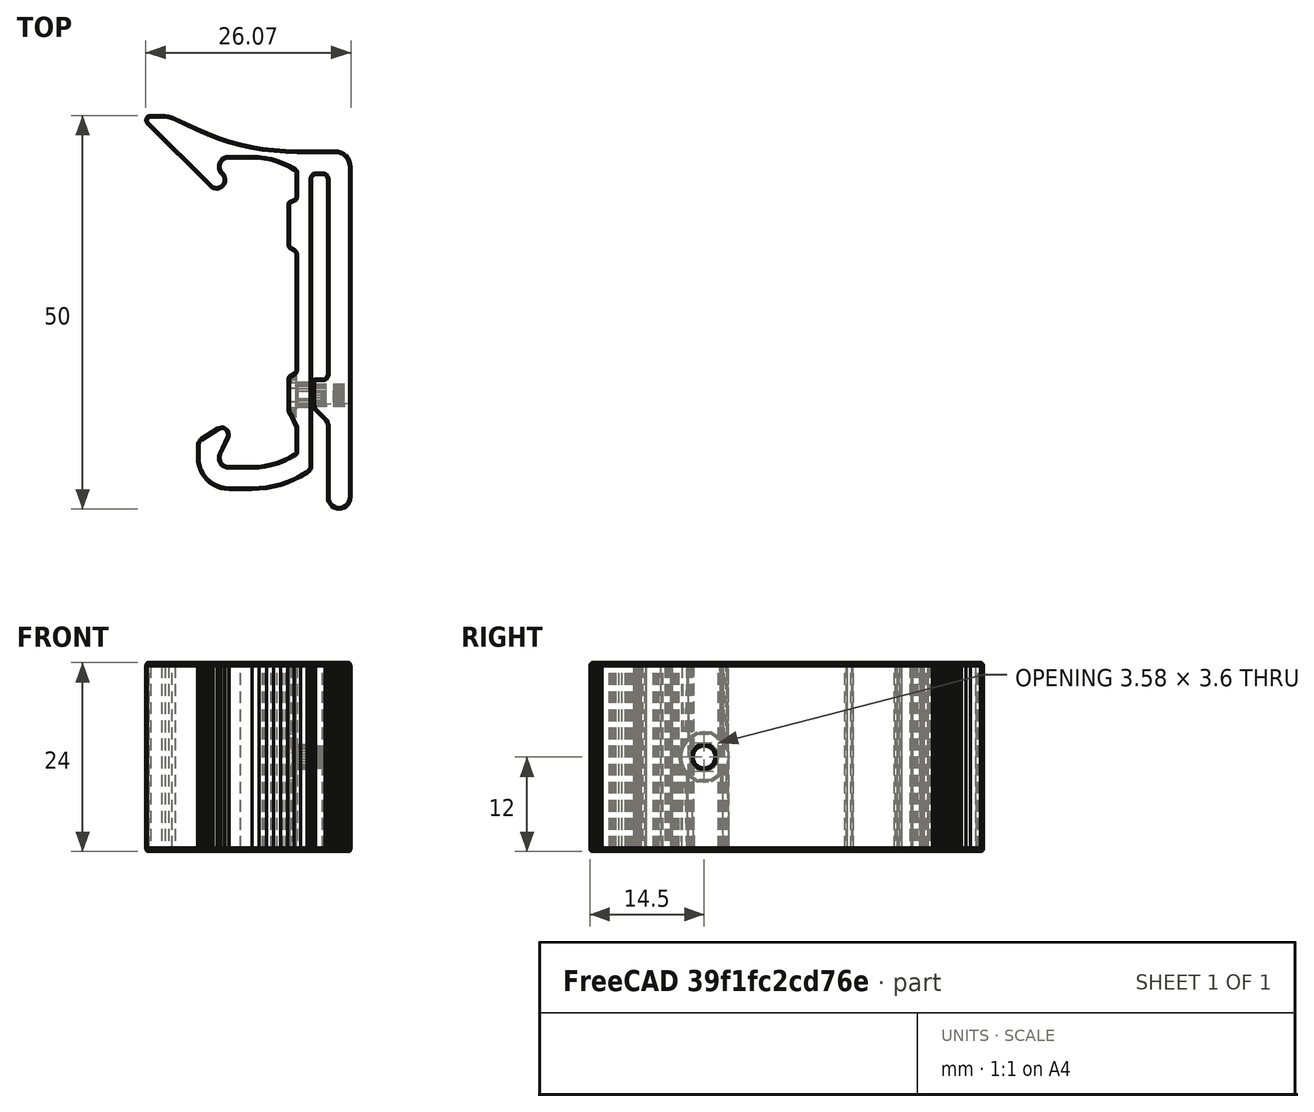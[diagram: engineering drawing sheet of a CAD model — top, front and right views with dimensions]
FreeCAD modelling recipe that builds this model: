
FCSTD DOCUMENT  (FreeCAD 0.21R33771 (Git))
Label: PenelopeClip
License: All rights reserved
LicenseURL: http://en.wikipedia.org/wiki/All_rights_reserved
objects: Part::Refine×1, PartDesign::FeatureBase×1, Sketcher::SketchObject×1, PartDesign::Body×1
note: 4 computed .brp shape members not serialized (recipe doc carries the construction recipe); baked Part::Feature solids carry a one-line shape summary decoded from their .brp

FEATURE [Part::Refine] Alley_Cat_TBeam_Molle_Clip001_solid001  label="Alley_Cat_TBeam_Molle_Clip001 (Solid)001"
FEATURE [PartDesign::FeatureBase] BaseFeature
  BaseFeature = -> Alley_Cat_TBeam_Molle_Clip001_solid001
FEATURE [Sketcher::SketchObject] Sketch
  FullyConstrained = true
  MapMode = 5
  Support = -> [XY_Plane]
  sketch-geometry (67):
    g0: LineSegment StartX=0 StartY=0 StartZ=0 EndX=0 EndY=42.04 EndZ=0
    g1: ArcOfCircle CenterX=-2 CenterY=42.04 CenterZ=0 NormalX=0 NormalY=0 NormalZ=1 AngleXU=0 Radius=2 StartAngle=1e-15 EndAngle=1.57049
    g2: LineSegment StartX=-1.99938 StartY=44.04 StartZ=0 EndX=-6.83938 EndY=44.0415 EndZ=0
    g3: LineSegment StartX=-6.83938 StartY=44.0415 StartZ=0 EndX=-8.29938 EndY=44.0804 EndZ=0
    g4: LineSegment StartX=-8.29938 StartY=44.0804 StartZ=0 EndX=-9.74938 EndY=44.1804 EndZ=0
    g5: LineSegment StartX=-9.74938 StartY=44.1804 StartZ=0 EndX=-11.1894 EndY=44.3604 EndZ=0
    g6: LineSegment StartX=-11.1894 StartY=44.3604 StartZ=0 EndX=-12.6294 EndY=44.6004 EndZ=0
    g7: LineSegment StartX=-12.6294 StartY=44.6004 StartZ=0 EndX=-14.0394 EndY=44.9204 EndZ=0
    g8: LineSegment StartX=-14.0394 StartY=44.9204 StartZ=0 EndX=-15.4494 EndY=45.3004 EndZ=0
    g9: LineSegment StartX=-15.4494 StartY=45.3004 StartZ=0 EndX=-16.8394 EndY=45.7504 EndZ=0
    g10: LineSegment StartX=-16.8394 StartY=45.7504 StartZ=0 EndX=-18.1994 EndY=46.2704 EndZ=0
    g11: LineSegment StartX=-18.1994 StartY=46.2704 StartZ=0 EndX=-19.5294 EndY=46.8504 EndZ=0
    g12: LineSegment StartX=-19.5294 StartY=46.8504 StartZ=0 EndX=-22.3294 EndY=48.1604 EndZ=0
    g13: ArcOfCircle CenterX=-24.0626 CenterY=44.4558 CenterZ=0 NormalX=0 NormalY=0 NormalZ=1 AngleXU=0 Radius=4.09 StartAngle=1.13319 EndAngle=1.51939
    g14: LineSegment StartX=-23.8525 StartY=48.5404 StartZ=0 EndX=-25.2925 EndY=48.5404 EndZ=0
    g15: ArcOfCircle CenterX=-25.2925 CenterY=47.9404 CenterZ=0 NormalX=0 NormalY=0 NormalZ=1 AngleXU=0 Radius=0.6 StartAngle=1.5708 EndAngle=3.9406
    g16: LineSegment StartX=-25.7109 StartY=47.5104 StartZ=0 EndX=-17.7309 EndY=39.5304 EndZ=0
    g17: ArcOfCircle CenterX=-16.8965 CenterY=40.3647 CenterZ=0 NormalX=0 NormalY=0 NormalZ=1 AngleXU=0 Radius=1.18 StartAngle=3.92699 EndAngle=6.83204
    g18: LineSegment StartX=-15.8898 StartY=40.9804 StartZ=0 EndX=-16.0498 EndY=41.2104 EndZ=0
    g19: LineSegment StartX=-16.0498 StartY=41.2104 StartZ=0 EndX=-16.1898 EndY=41.3504 EndZ=0
    g20: ArcOfCircle CenterX=-15.5181 CenterY=42.0221 CenterZ=0 NormalX=0 NormalY=0 NormalZ=1 AngleXU=0 Radius=0.95 StartAngle=2.92059 EndAngle=3.92699
    g21: ArcOfCircle CenterX=-15.3132 CenterY=41.9761 CenterZ=0 NormalX=0 NormalY=0 NormalZ=1 AngleXU=0 Radius=1.16 StartAngle=1.67012 EndAngle=2.92059
    g22: LineSegment StartX=-15.4282 StartY=43.1304 StartZ=0 EndX=-12.4682 EndY=43.1304 EndZ=0
    g23: ArcOfCircle CenterX=-12.4682 CenterY=33.0904 CenterZ=0 NormalX=0 NormalY=0 NormalZ=1 AngleXU=0 Radius=10.04 StartAngle=1.0134 EndAngle=1.5708
    g24: LineSegment StartX=-7.1573 StartY=41.6107 StartZ=0 EndX=-7.10385 EndY=41.5774 EndZ=0
    g25: ArcOfCircle CenterX=-7.20965 CenterY=41.4076 CenterZ=0 NormalX=0 NormalY=0 NormalZ=1 AngleXU=0 Radius=0.2 StartAngle=0.0595829 EndAngle=1.0134
    g26: LineSegment StartX=-7.01 StartY=41.4195 StartZ=0 EndX=-7.01 EndY=38.2495 EndZ=0
    g27: ArcOfCircle CenterX=-7.4 CenterY=38.2495 CenterZ=0 NormalX=0 NormalY=0 NormalZ=1 AngleXU=0 Radius=0.39 StartAngle=5.10718 EndAngle=6.28319
    g28: LineSegment StartX=-7.25 StartY=37.8895 StartZ=0 EndX=-7.78 EndY=37.6395 EndZ=0
    g29: ArcOfCircle CenterX=-7.60935 CenterY=37.2778 CenterZ=0 NormalX=0 NormalY=0 NormalZ=1 AngleXU=0 Radius=0.4 StartAngle=2.01155 EndAngle=3.35826
    g30: LineSegment StartX=-8 StartY=37.1918 StartZ=0 EndX=-8 EndY=31.9818 EndZ=0
    g31: ArcOfCircle CenterX=-7.6 CenterY=31.9818 CenterZ=0 NormalX=0 NormalY=0 NormalZ=1 AngleXU=0 Radius=0.4 StartAngle=3.14159 EndAngle=4.1509
    g32: LineSegment StartX=-7.81298 StartY=31.6432 StartZ=0 EndX=-7.19298 EndY=31.2532 EndZ=0
    g33: ArcOfCircle CenterX=-7.39531 CenterY=30.9315 CenterZ=0 NormalX=0 NormalY=0 NormalZ=1 AngleXU=0 Radius=0.38 StartAngle=6.23489 EndAngle=7.29249
    g34: LineSegment StartX=-7.01575 StartY=30.9132 StartZ=0 EndX=-7.01575 EndY=16.1232 EndZ=0
    g35: ArcOfCircle CenterX=-7.38575 CenterY=16.1232 CenterZ=0 NormalX=0 NormalY=0 NormalZ=1 AngleXU=0 Radius=0.37 StartAngle=5.24441 EndAngle=6.28319
    g36: LineSegment StartX=-7.19806 StartY=15.8043 StartZ=0 EndX=-7.81806 EndY=15.4043 EndZ=0
    g37: ArcOfCircle CenterX=-7.59579 CenterY=15.0598 CenterZ=0 NormalX=0 NormalY=0 NormalZ=1 AngleXU=0 Radius=0.41 StartAngle=2.14376 EndAngle=3.15495
    g38: LineSegment StartX=-8.00575 StartY=15.0543 StartZ=0 EndX=-8.00575 EndY=11.1143 EndZ=0
    g39: ArcOfCircle CenterX=-7.46575 CenterY=11.1143 CenterZ=0 NormalX=0 NormalY=0 NormalZ=1 AngleXU=0 Radius=0.54 StartAngle=3.14159 EndAngle=3.73722
    g40: LineSegment StartX=-7.91277 StartY=10.8114 StartZ=0 EndX=-7.57277 EndY=10.1814 EndZ=0
    g41: LineSegment StartX=-7.57277 StartY=10.1814 StartZ=0 EndX=-7.26277 EndY=9.53138 EndZ=0
    g42: LineSegment StartX=-7.26277 StartY=9.53138 StartZ=0 EndX=-7.00277 EndY=8.90138 EndZ=0
    g43: LineSegment StartX=-7.00277 StartY=8.90138 StartZ=0 EndX=-7.00277 EndY=5.71138 EndZ=0
    g44: ArcOfCircle CenterX=-7.20277 CenterY=5.71138 CenterZ=0 NormalX=0 NormalY=0 NormalZ=1 AngleXU=0 Radius=0.2 StartAngle=5.28586 EndAngle=6.28319
    g45: LineSegment StartX=-7.09426 StartY=5.54337 StartZ=0 EndX=-7.86426 EndY=5.10337 EndZ=0
    g46: LineSegment StartX=-7.86426 StartY=5.10337 StartZ=0 EndX=-8.59426 EndY=4.74337 EndZ=0
    g47: LineSegment StartX=-8.59426 StartY=4.74337 StartZ=0 EndX=-9.36426 EndY=4.45337 EndZ=0
    g48: LineSegment StartX=-9.36426 StartY=4.45337 StartZ=0 EndX=-10.1543 EndY=4.22337 EndZ=0
    g49: LineSegment StartX=-10.1543 StartY=4.22337 StartZ=0 EndX=-10.9543 EndY=4.05337 EndZ=0
    g50: LineSegment StartX=-10.9543 StartY=4.05337 StartZ=0 EndX=-11.7643 EndY=3.95489 EndZ=0
    g51: LineSegment StartX=-11.7643 StartY=3.95489 StartZ=0 EndX=-12.5743 EndY=3.91785 EndZ=0
    g52: LineSegment StartX=-12.5743 StartY=3.91785 StartZ=0 EndX=-15.5443 EndY=3.91785 EndZ=0
    g53: ArcOfCircle CenterX=-15.5443 CenterY=5.01785 CenterZ=0 NormalX=0 NormalY=0 NormalZ=1 AngleXU=0 Radius=1.1 StartAngle=2.71189 EndAngle=4.71239
    g54: LineSegment StartX=-16.5443 StartY=5.47611 StartZ=0 EndX=-15.5443 EndY=7.58611 EndZ=0
    g55: ArcOfCircle CenterX=-16.4118 CenterY=7.99725 CenterZ=0 NormalX=0 NormalY=0 NormalZ=1 AngleXU=0 Radius=0.96 StartAngle=5.84061 EndAngle=8.42102
    g56: LineSegment StartX=-16.9274 StartY=8.80701 StartZ=0 EndX=-19.0474 EndY=7.45701 EndZ=0
    g57: ArcOfCircle CenterX=-18.5049 CenterY=6.60508 CenterZ=0 NormalX=0 NormalY=0 NormalZ=1 AngleXU=0 Radius=1.01 StartAngle=2.13783 EndAngle=3.1405
    g58: LineSegment StartX=-19.5149 StartY=6.60618 StartZ=0 EndX=-19.5166 EndY=5.02618 EndZ=0
    g59: ArcOfCircle CenterX=-15.5066 CenterY=5.02179 CenterZ=0 NormalX=0 NormalY=0 NormalZ=1 AngleXU=0 Radius=4.01 StartAngle=3.1405 EndAngle=4.7137
    g60: LineSegment StartX=-15.5014 StartY=1.01179 StartZ=0 EndX=-12.5814 EndY=1.01562 EndZ=0
    g61: ArcOfCircle CenterX=-12.5986 CenterY=14.1356 CenterZ=0 NormalX=0 NormalY=0 NormalZ=1 AngleXU=0 Radius=13.12 StartAngle=4.7137 EndAngle=5.27671
    g62: ArcOfCircle CenterX=-6.2768 CenterY=4.14825 CenterZ=0 NormalX=0 NormalY=0 NormalZ=1 AngleXU=0 Radius=1.3 StartAngle=5.27671 EndAngle=6.12215
    g63: LineSegment StartX=-4.99361 StartY=3.93981 StartZ=0 EndX=-4.99361 EndY=14.9198 EndZ=0
    g64: ArcOfCircle CenterX=-4.89575 CenterY=14.9198 CenterZ=0 NormalX=0 NormalY=0 NormalZ=1 AngleXU=0 Radius=0.09786 StartAngle=0.207791 EndAngle=3.14159
    g65: LineSegment StartX=-4.8 StartY=14.94 StartZ=0 EndX=-4.8 EndY=0 EndZ=0
    g66: LineSegment StartX=-4.8 StartY=0 StartZ=0 EndX=0 EndY=0 EndZ=0
  constraints (194):
    c: Vertical(g0)
    c: Tangent(g0,g1) = -1.5708
    c: Tangent(g1,g2) = -1.5708
    c: Coincident(g2,g3)
    c: Coincident(g3,g4)
    c: Coincident(g4,g5)
    c: Coincident(g5,g6)
    c: Coincident(g6,g7)
    c: Coincident(g7,g8)
    c: Coincident(g8,g9)
    c: Coincident(g9,g10)
    c: Coincident(g10,g11)
    c: Coincident(g11,g12)
    c: Tangent(g12,g13) = -1.5708
    c: Coincident(g13,g14)
    c: Horizontal(g14)
    c: Tangent(g14,g15) = -1.5708
    c: Coincident(g15,g16)
    c: Tangent(g16,g17) = -1.5708
    c: Coincident(g17,g18)
    c: Coincident(g18,g19)
    c: Tangent(g19,g20) = 1.5708
    c: Tangent(g20,g21) = -1.5708
    c: Coincident(g21,g22)
    c: Horizontal(g22)
    c: Tangent(g22,g23) = 1.5708
    c: Tangent(g23,g24) = 1.5708
    c: Tangent(g24,g25) = 1.5708
    c: Coincident(g25,g26)
    c: Vertical(g26)
    c: Tangent(g26,g27) = 1.5708
    c: Coincident(g27,g28)
    c: Tangent(g28,g29) = -1.5708
    c: Coincident(g29,g30)
    c: Vertical(g30)
    c: Tangent(g30,g31) = -1.5708
    c: Tangent(g31,g32) = -1.5708
    c: Tangent(g32,g33) = 1.5708
    c: Coincident(g33,g34)
    c: Vertical(g34)
    c: Tangent(g34,g35) = 1.5708
    c: Coincident(g35,g36)
    c: Tangent(g36,g37) = -1.5708
    c: Coincident(g37,g38)
    c: Vertical(g38)
    c: Tangent(g38,g39) = -1.5708
    c: Coincident(g39,g40)
    c: Coincident(g40,g41)
    c: Coincident(g41,g42)
    c: Coincident(g42,g43)
    c: Vertical(g43)
    c: Tangent(g43,g44) = 1.5708
    c: Coincident(g44,g45)
    c: Coincident(g45,g46)
    c: Coincident(g46,g47)
    c: Coincident(g47,g48)
    c: Coincident(g48,g49)
    c: Coincident(g49,g50)
    c: Coincident(g50,g51)
    c: Coincident(g51,g52)
    c: Horizontal(g52)
    c: Tangent(g52,g53) = 1.5708
    c: Coincident(g53,g54)
    c: Tangent(g54,g55) = -1.5708
    c: Tangent(g55,g56) = -1.5708
    c: Tangent(g56,g57) = -1.5708
    c: Tangent(g57,g58) = -1.5708
    c: Tangent(g58,g59) = -1.5708
    c: Tangent(g59,g60) = -1.5708
    c: Tangent(g60,g61) = -1.5708
    c: Tangent(g61,g62) = -1.5708
    c: Coincident(g62,g63)
    c: Vertical(g63)
    c: Tangent(g63,g64) = 1.5708
    c: Coincident(g64,g65)
    c: Vertical(g65)
    c: Coincident(g65,g66)
    c: Coincident(g66,g0)
    c: Horizontal(g66)
    c: Radius(g1) = 2
    c: Radius(g15) = 0.6
    c: Radius(g17) = 1.18
    c: Radius(g20) = 0.95
    c: Radius(g21) = 1.16
    c: Radius(g25) = 0.2
    c: Radius(g27) = 0.39
    c: Radius(g29) = 0.4
    c: Radius(g31) = 0.4
    c: Radius(g33) = 0.38
    c: Radius(g35) = 0.37
    c: Radius(g37) = 0.41
    c: Radius(g39) = 0.54
    c: Radius(g44) = 0.2
    c: Radius(g55) = 0.96
    c: Radius(g57) = 1.01
    c: Radius(g53) = 1.1
    c: Radius(g59) = 4.01
    c: Radius(g61) = 13.12
    c: Radius(g62) = 1.3
    c: Radius(g64) = 0.09786
    c: DistanceY(g0,g0) = 42.04
    c: DistanceY(g65,g65) = 14.94
    c: DistanceY(g63,g63) = 10.98
    c: DistanceY(g45,g45) = 0.44
    c: DistanceY(g46,g46) = 0.36
    c: DistanceY(g47,g47) = 0.29
    c: DistanceY(g48,g48) = 0.23
    c: DistanceY(g49,g49) = 0.17
    c: DistanceY(g50,g50) = 0.09848
    c: DistanceY(g51,g51) = 0.03704
    c: DistanceY(g54,g54) = 2.11
    c: DistanceY(g56,g56) = 1.35
    c: DistanceY(g58,g58) = 1.58
    c: DistanceY(g38,g38) = 3.94
    c: DistanceY(g40,g40) = 0.63
    c: DistanceY(g41,g41) = 0.65
    c: DistanceY(g42,g42) = 0.63
    c: DistanceY(g34,g34) = 14.79
    c: DistanceY(g32,g32) = 0.39
    c: DistanceY(g30,g30) = 5.21
    c: DistanceY(g26,g26) = 3.17
    c: DistanceY(g16,g16) = 7.98
    c: Radius(g13) = 4.09
    c: DistanceY(g12,g12) = 1.31
    c: DistanceY(g11,g11) = 0.58
    c: DistanceY(g10,g10) = 0.52
    c: DistanceY(g9,g9) = 0.45
    c: DistanceY(g8,g8) = 0.38
    c: DistanceY(g7,g7) = 0.32
    c: DistanceY(g6,g6) = 0.24
    c: DistanceY(g5,g5) = 0.18
    c: DistanceY(g4,g4) = 0.1
    c: DistanceY(g3,g3) = 0.03887
    c: DistanceY(g2,g2) = 0.00149
    c: Radius(g23) = 10.04
    c: DistanceX(g66,g66) = 4.8
    c: DistanceX(g60,g60) = 2.92
    c: DistanceY(g60,g60) = 0.00383
    c: DistanceX(g58,g58) = 0.00173
    c: DistanceX(g56,g56) = 2.12
    c: DistanceX(g54,g54) = 1
    c: DistanceX(g52,g52) = 2.97
    c: DistanceX(g51,g51) = 0.81
    c: DistanceX(g50,g50) = 0.81
    c: DistanceX(g49,g49) = 0.8
    c: DistanceX(g48,g48) = 0.79
    c: DistanceX(g47,g47) = 0.77
    c: DistanceX(g46,g46) = 0.73
    c: DistanceX(g45,g45) = 0.77
    c: DistanceX(g42,g42) = 0.26
    c: DistanceX(g41,g41) = 0.31
    c: DistanceX(g40,g40) = 0.34
    c: DistanceX(g36,g36) = 0.62
    c: DistanceY(g36,g36) = 0.4
    c: DistanceX(g32,g32) = 0.62
    c: DistanceX(g28,g28) = 0.53
    c: DistanceY(g28,g28) = 0.25
    c: DistanceX(g22,g22) = 2.96
    c: DistanceX(g19,g19) = 0.14
    c: DistanceX(g18,g18) = 0.16
    c: DistanceY(g19,g19) = 0.14
    c: DistanceY(g18,g18) = 0.23
    c: DistanceX(g16,g16) = 7.98
    c: DistanceX(g14,g14) = 1.44
    c: DistanceX(g12,g12) = 2.8
    c: DistanceX(g11,g11) = 1.33
    c: DistanceX(g10,g10) = 1.36
    c: DistanceX(g9,g9) = 1.39
    c: DistanceX(g8,g8) = 1.41
    c: DistanceX(g7,g7) = 1.41
    c: DistanceX(g6,g6) = 1.44
    c: DistanceX(g5,g5) = 1.44
    c: DistanceX(g4,g4) = 1.45
    c: DistanceX(g3,g3) = 1.46
    c: DistanceX(g2,g2) = 4.84
    c: DistanceX(g53,g52) = 1
    c: DistanceY(g61,g62) = 0.89
    c: DistanceY(g64,g37) = 0.14
    c: DistanceY(g37,g36) = 0.35
    c: DistanceY(g43,g43) = 3.19
    c: DistanceX(g25,g1) = 5.01
    c: DistanceY(g20,g21) = 0.9
    c: DistanceY(g19,g20) = 0.88
    c: DistanceY(g16,g17) = 1.45
    c: DistanceY(g15,g14) = 1.03
    c: DistanceY(g12,g13) = 0.38
    c: DistanceY(g33,g32) = 0.34
    c: DistanceX(g29,g0) = 8
    c: DistanceX(g34,g64) = 2.12
    c: DistanceX(g37,g64) = 3.11
    c: DistanceX(g29,g28) = 0.22
    c: DistanceX(g24,g25) = 0.09385
    c: DistanceX(g44,g43) = 0.09149
    c: Coincident(g0,g-1)
FEATURE [PartDesign::Body] Body
  BaseFeature = -> Alley_Cat_TBeam_Molle_Clip001_solid001
  Group = -> [BaseFeature,Sketch]
  Origin = -> Origin
  Tip = -> BaseFeature
